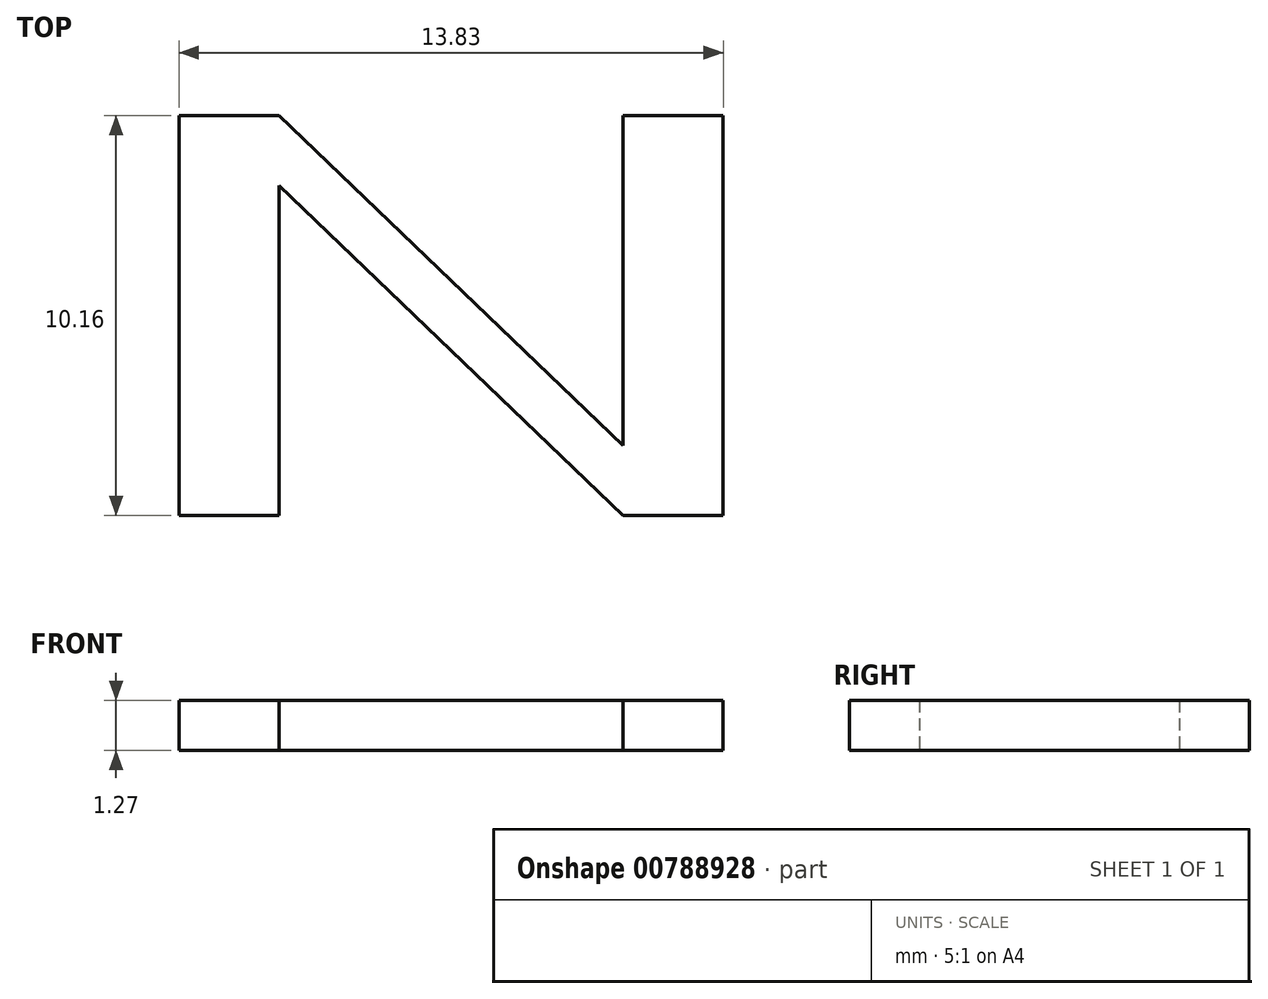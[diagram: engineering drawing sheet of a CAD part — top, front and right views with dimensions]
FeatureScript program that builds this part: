
annotation { "Feature Type Name" : "Feature", "Feature Type Description" : "" }
export const myFeature = defineFeature(function(context is Context, id is Id, definition is map)
    precondition{}
    {
        {
            var Q0;
            Q0=qCreatedBy(makeId("Top.planeOp"),FACE);
            var sketch = newSketch(context, id + "F0", { "sketchPlane" : qUnion([Q0])});
            skLineSegment(sketch, "E0.bottom", {"start": v(-6.65, 4.2) * mm, "end": v(-4.1, 4.2) * mm});
            skLineSegment(sketch, "E0.top", {"start": v(-6.65, -5.96) * mm, "end": v(-4.1, -5.96) * mm});
            skLineSegment(sketch, "E0.left", {"start": v(-6.65, 4.2) * mm, "end": v(-6.65, -5.96) * mm});
            skLineSegment(sketch, "E0.right", {"start": v(-4.1, 4.2) * mm, "end": v(-4.1, -5.96) * mm});
            skLineSegment(sketch, "E1.bottom", {"start": v(4.64, 4.2) * mm, "end": v(7.18, 4.2) * mm});
            skLineSegment(sketch, "E1.top", {"start": v(4.64, -5.96) * mm, "end": v(7.18, -5.96) * mm});
            skLineSegment(sketch, "E1.left", {"start": v(4.64, 4.2) * mm, "end": v(4.64, -5.96) * mm});
            skLineSegment(sketch, "E1.right", {"start": v(7.18, 4.2) * mm, "end": v(7.18, -5.96) * mm});
            skLineSegment(sketch, "E2", {"start": v(-4.1, 2.42) * mm, "end": v(4.64, -5.96) * mm});
            skLineSegment(sketch, "E3", {"start": v(-4.1, 4.2) * mm, "end": v(4.64, -4.18) * mm});
            skSolve(sketch);
        }
        {
            var Q0;
            Q0 = qSketchRegion(id + "F0", true);
            extrude(context, id + "F1", {"entities" : qUnion([Q0]), "depth" : 1.27 * mm, "offsetDistance" : 25.4 * mm});
        }
    });
